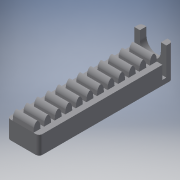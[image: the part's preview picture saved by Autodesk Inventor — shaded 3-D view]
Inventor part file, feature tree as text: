
AUTODESK INVENTOR PART (.ipt)
format: ipt  version: 2018 (Build 220112000, 112)  size: 478,208 bytes
history: native  units: in
note: dims shown in document units (in); Inventor stores cm internally (conversion verified against a paired STEP export)
features: extrude x15, sketch x14, projected_geometry x5, other x4, reference x2, fillet x1
ambient origin geometry x8: Origin, YZ Plane, XZ Plane, XY Plane, X Axis, Y Axis, Z Axis, Center Point
bodies: Body1 (feature_tree)
feature tree (41):
  extrude  "Extrusion2"  Depth=0.435in
  sketch  "Sketch3"  dims[d6=0.385in d7=0.0in d9=0.092in]
  extrude  "Extrusion6"  Depth=0.385in
  extrude  "Extrusion7"  Depth=0.1in
  extrude  "Extrusion8"  Depth=0.385in
  extrude  "Extrusion9"  Depth=0.3937in
  extrude  "Extrusion10"  Depth=0.25in
  extrude  "Extrusion11"  Depth=0.385in
  extrude  "Extrusion12"  Depth=0.4in
  extrude  "Extrusion13"  Depth=0.385in TaperAngle=0.0deg
  extrude  "Extrusion14"  Depth=2.5in
  extrude  "Extrusion15"  Depth=0.25in
  extrude  "Extrusion16"  Depth=0.0394in TaperAngle=0.0deg
  extrude  "Extrusion17"  Depth=0.0984in
  extrude  "Extrusion18"  Depth=0.0394in TaperAngle=0.0deg
  extrude  "Extrusion19"  Depth=0.0591in
  fillet  "Fillet2"  Radius=0.0472in
  sketch  "Sketch2"  dims[d4=2.5in d5=0.435in]
  sketch  "Sketch5"  dims[d58=0.1in d59=0.0in d60=0.1in]
  projected_geometry  "Projected Loop1"
  projected_geometry  "Projected Loop2"
  projected_geometry  "Projected Loop3"
  sketch  "Sketch7"  dims[d61=0.385in d62=0.0in d63=0.5814in]
  sketch  "Sketch8"  dims[d64=0.5814in d72=7.874in d74=0.1271in d75=0.3937in d77=1.0in]
  sketch  "Sketch9"  dims[d79=0.25in d80=0.0in d81=0.05in]
  sketch  "Sketch10"  dims[d82=0.385in d83=0.0in d84=0.15in]
  sketch  "Sketch11"  dims[d85=0.05in d86=0.4in]
  projected_geometry  "Projected Loop5"
  sketch  "Sketch12"  dims[d87=0.385in d88=0.0in d89=0.385in d90=0.0in]
  projected_geometry  "Projected Loop6"
  sketch  "Sketch13"  dims[d91=1.0in d92=0.0in d93=2.5in]
  sketch  "Sketch14"  dims[d95=0.1378in d96=0.0in d97=0.25in]
  sketch  "Sketch15"  dims[d98=0.25in d99=0.0394in d100=0.0in]
  sketch  "Sketch16"  dims[d101=0.0984in d102=0.0984in]
  reference  "Reference1"
  sketch  "Sketch17"  dims[d103=0.0394in d104=0.0in d106=1.0in d107=0.0in d108=0.0591in d109=0.0472in d110=0.0in d111=0.1177in d112=0.1177in d113=0.3937in d114=0.3937in d115=0.0787in d116=0.0in d117=1.0in d118=0.0in d119=0.0394in]
  reference  "Reference2"
  other  "<userpath>\OneDrive\Documents\Inventor\TSA\2018\Animatronics\Tortoise\TurtleAssembly2.iam"
  other  "TurtleAssembly2.iam"
  other  "SyringEnd:5"
  other  "SyringEnd:4"
